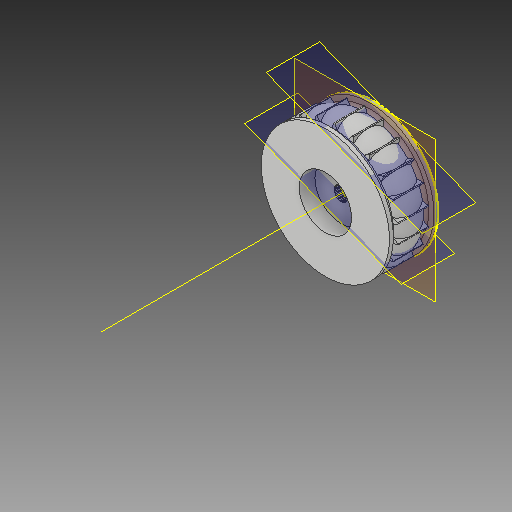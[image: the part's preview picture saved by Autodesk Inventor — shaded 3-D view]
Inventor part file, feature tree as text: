
AUTODESK INVENTOR PART (.ipt)
format: ipt  version: 2017 (Build 210142000, 142)  size: 626,688 bytes
history: native  units: mm
features: sketch x7, other x4, plane x4
ambient origin geometry x8: Origin, YZ Plane, XZ Plane, XY Plane, X Axis, Y Axis, Z Axis, Center Point
bodies: Solid1 (feature_tree)
feature tree (15):
  other  "rear-wheel.ipt"
  other  "Solid1::rear-wheel.ipt"
  other  "TaggingFeature1"
  sketch  "Sketch1"  dims[d0=10.0mm]
  sketch  "Sketch2"
  sketch  "Sketch3"
  sketch  "Sketch5"
  sketch  "Sketch6"
  sketch  "Sketch7"
  sketch  "Sketch8"
  plane  "Work Plane1"
  plane  "Work Plane2"
  plane  "Work Plane3"
  plane  "Work Plane4"
  other  "Work Axis1"
